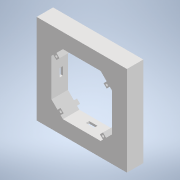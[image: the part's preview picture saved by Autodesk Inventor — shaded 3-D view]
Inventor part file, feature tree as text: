
AUTODESK INVENTOR PART (.ipt)
format: ipt  version: 2021.2 (Build 252289000, 289)  size: 273,920 bytes
history: native  units: mm
features: reference x22, extrude x7, sketch x7, other x6
ambient origin geometry x8: Origin, YZ Plane, XZ Plane, XY Plane, X Axis, Y Axis, Z Axis, Center Point
bodies: Body1 (feature_tree)
feature tree (42):
  other  "Твердое тело1"
  extrude  "Выдавливание1"  Depth=2.5mm
  extrude  "Выдавливание2"  Depth=2.0mm
  sketch  "Эскиз3"
  other  "РабПлоскость1"
  extrude  "Выдавливание3"  Depth=13.0mm TaperAngle=0.0deg
  extrude  "Выдавливание4"  Depth=2.0mm
  extrude  "Выдавливание5"  Depth=2.0mm
  extrude  "Выдавливание6"  Depth=2.0mm TaperAngle=0.0deg
  extrude  "Выдавливание7"  Depth=9.0mm
  sketch  "Эскиз1"
  reference  "Ссылка1"
  sketch  "Эскиз2"
  reference  "Ссылка2"
  reference  "Ссылка3"
  reference  "Ссылка4"
  reference  "Ссылка5"
  reference  "Ссылка6"
  reference  "Ссылка7"
  reference  "Ссылка8"
  reference  "Ссылка9"
  reference  "Ссылка10"
  reference  "Ссылка11"
  reference  "Ссылка12"
  reference  "Ссылка13"
  reference  "Ссылка14"
  reference  "Ссылка15"
  reference  "Ссылка16"
  reference  "Ссылка17"
  reference  "Ссылка18"
  sketch  "Эскиз4"
  reference  "Ссылка19"
  sketch  "Эскиз5"
  reference  "Ссылка20"
  sketch  "Эскиз6"
  reference  "Ссылка21"
  sketch  "Эскиз7"
  reference  "Ссылка22"
  parser-record x1  (decoder bookkeeping rows leaked as tree rows — omitted from the tree; the rows remain in map.json)
  other  "Сборка1.iam"
  other  "Середина:1"
  other  "Верх:1"
note: 1 file-system path scrubbed to <path> (originals preserved in map.json)
